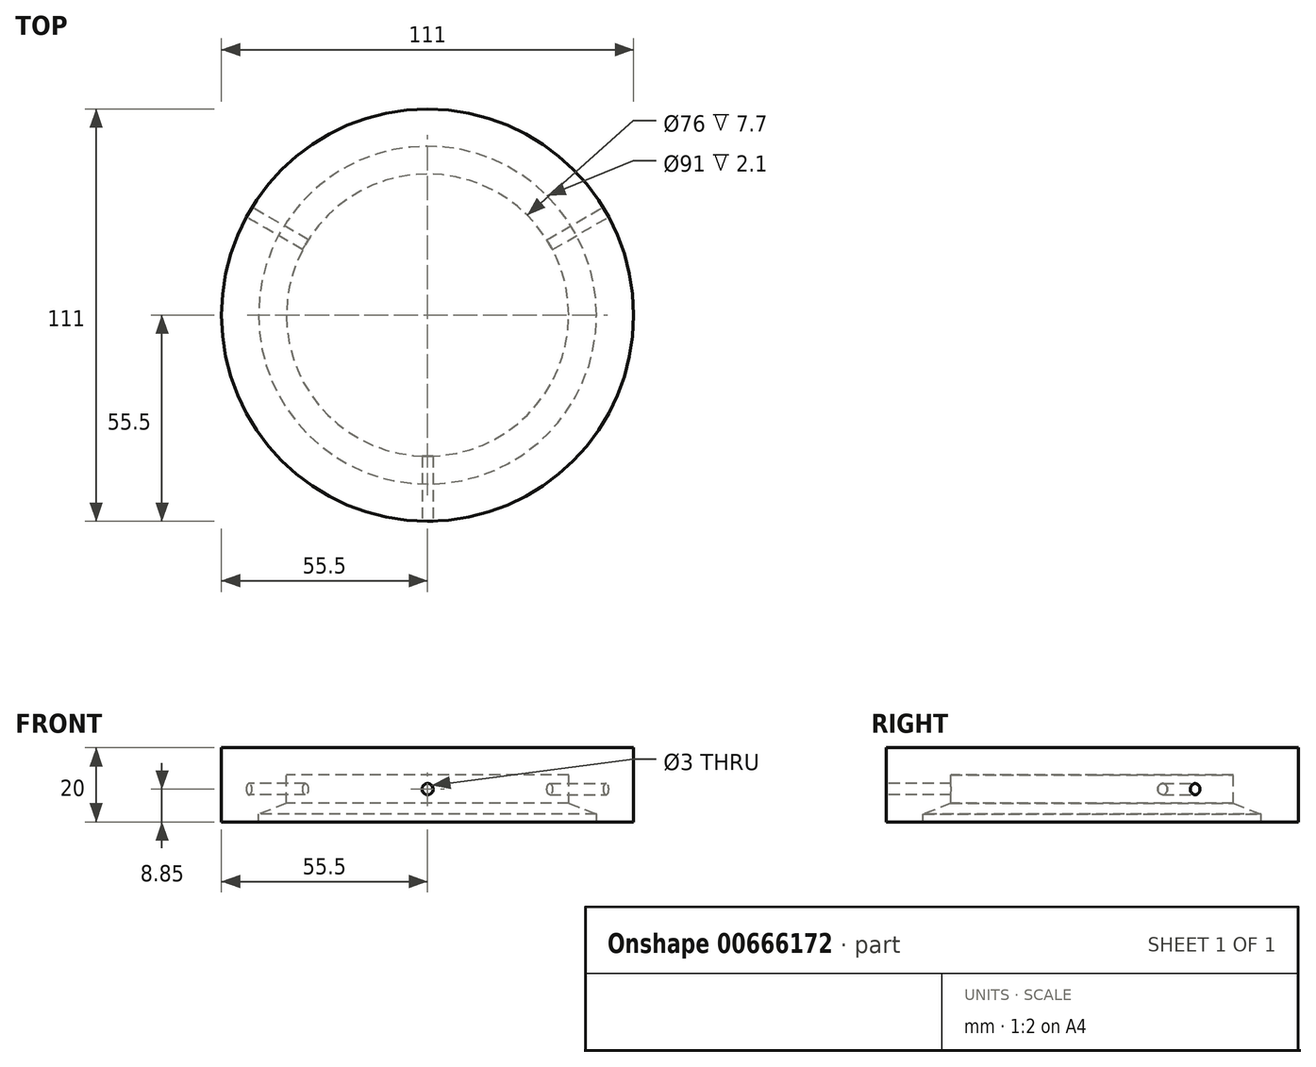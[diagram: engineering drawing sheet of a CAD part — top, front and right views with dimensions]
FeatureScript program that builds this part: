
annotation { "Feature Type Name" : "Feature", "Feature Type Description" : "" }
export const myFeature = defineFeature(function(context is Context, id is Id, definition is map)
    precondition{}
    {
        {
            var Q0;
            Q0=qCreatedBy(makeId("Right.planeOp"),FACE);
            var sketch = newSketch(context, id + "F0", { "sketchPlane" : qUnion([Q0])});
            skLineSegment(sketch, "E0", {"start": v(-45.5, 0) * mm, "end": v(-45.5, 2.1) * mm});
            skLineSegment(sketch, "E1", {"start": v(-45.5, 2.1) * mm, "end": v(-38, 5) * mm});
            skLineSegment(sketch, "E2", {"start": v(-38, 5) * mm, "end": v(-38, 12.7) * mm});
            skLineSegment(sketch, "E3", {"start": v(0, 23.43) * mm, "end": v(0, -29.1) * mm, "construction": true});
            skLineSegment(sketch, "E4", {"start": v(-55.5, 0) * mm, "end": v(-55.5, 20) * mm});
            skLineSegment(sketch, "E5", {"start": v(-38, 12.7) * mm, "end": v(0, 12.7) * mm});
            skLineSegment(sketch, "E6", {"start": v(-55.5, 20) * mm, "end": v(0, 20) * mm});
            skLineSegment(sketch, "E7", {"start": v(0, 20) * mm, "end": v(0, 12.7) * mm});
            skLineSegment(sketch, "E8", {"start": v(-45.5, 0) * mm, "end": v(-55.5, 0) * mm});
            skSolve(sketch);
        }
        {
            var Q0;
            Q0=makeQuery(id+"F0.imprint","IMPRINT",FACE,{"disambiguationData":[TD([[makeQuery(id+"F0.imprint","IMPRINT",EDGE,{"derivedFrom":sQuery(id+"F0.wireOp",EDGE,"E0")}),1.0]])]});
            var Q1;
            Q1=sQuery(id+"F0.wireOp",EDGE,"E3");
            revolve(context, id + "F1", {"entities" : qUnion([Q0]), "axis" : qUnion([Q1]), "revolveType" : RevolveType.FULL});
        }
        {
            var Q0;
            Q0=qCreatedBy(makeId("Top.planeOp"),FACE);
            cPlane(context, id + "F2", {"entities" : qUnion([Q0]), "cplaneType" : CPlaneType.OFFSET, "offset" : 8.85 * mm, "width" : 150 * mm, "height" : 150 * mm});
        }
        {
            var Q0;
            Q0=qCreatedBy(id+"F2.planeOp",FACE);
            var sketch = newSketch(context, id + "F3", { "sketchPlane" : qUnion([Q0])});
            skLineSegment(sketch, "E9", {"start": v(0, 0) * mm, "end": v(0, -55.5) * mm, "construction": true});
            skLineSegment(sketch, "E10.1.0", {"start": v(0, 0) * mm, "end": v(-48.06, 27.75) * mm, "construction": true});
            skLineSegment(sketch, "E10.2.0", {"start": v(0, 0) * mm, "end": v(48.06, 27.75) * mm, "construction": true});
            skPoint(sketch, "E10.center", {"position": v(0, 0) * mm});
            skLineSegment(sketch, "E10.anchor2", {"start": v(0, 0) * mm, "end": v(48.06, 27.75) * mm, "construction": true});
            skSolve(sketch);
        }
        {
            var Q0;
            Q0=sQuery(id+"F3.wireOp",VERTEX,"E9.end");
            var Q1;
            Q1=sQuery(id+"F3.wireOp",EDGE,"E9");
            cPlane(context, id + "F4", {"entities" : qUnion([Q0, Q1]), "cplaneType" : CPlaneType.LINE_POINT, "offset" : 25 * mm, "width" : 150 * mm, "height" : 150 * mm});
        }
        {
            var Q0;
            Q0=sQuery(id+"F3.wireOp",VERTEX,"E10.2.0.end");
            var Q1;
            Q1=sQuery(id+"F3.wireOp",EDGE,"E10.anchor2");
            cPlane(context, id + "F5", {"entities" : qUnion([Q0, Q1]), "cplaneType" : CPlaneType.LINE_POINT, "offset" : 25 * mm, "width" : 150 * mm, "height" : 150 * mm});
        }
        {
            var Q0;
            Q0=sQuery(id+"F3.wireOp",VERTEX,"E10.1.0.end");
            var Q1;
            Q1=sQuery(id+"F3.wireOp",EDGE,"E10.1.0");
            cPlane(context, id + "F6", {"entities" : qUnion([Q0, Q1]), "cplaneType" : CPlaneType.LINE_POINT, "offset" : 25 * mm, "width" : 150 * mm, "height" : 150 * mm});
        }
        {
            var Q0;
            Q0=qCreatedBy(id+"F5.planeOp",FACE);
            var sketch = newSketch(context, id + "F7", { "sketchPlane" : qUnion([Q0])});
            skCircle(sketch, "E11", {"center": v(0, 8.85) * mm, "radius": 1.5 * mm});
            skSolve(sketch);
        }
        {
            var Q0;
            Q0=qCreatedBy(id+"F6.planeOp",FACE);
            var sketch = newSketch(context, id + "F8", { "sketchPlane" : qUnion([Q0])});
            skCircle(sketch, "E12", {"center": v(0, 8.85) * mm, "radius": 1.5 * mm});
            skSolve(sketch);
        }
        {
            var Q0;
            Q0=qCreatedBy(id+"F4.planeOp",FACE);
            var sketch = newSketch(context, id + "F9", { "sketchPlane" : qUnion([Q0])});
            skCircle(sketch, "E13", {"center": v(0, 8.85) * mm, "radius": 1.5 * mm});
            skSolve(sketch);
        }
        {
            var Q0;
            Q0 = qSketchRegion(id + "F7", true);
            extrude(context, id + "F10", {"entities" : qUnion([Q0]), "operationType" : NewBodyOperationType.REMOVE, "endBound" : BoundingType.UP_TO_NEXT, "oppositeDirection" : true, "depth" : 25 * mm, "offsetDistance" : 25 * mm});
        }
        {
            var Q0;
            Q0 = qSketchRegion(id + "F8", true);
            var Q1;
            Q1=sQuery(id+"F8.wireOp",EDGE,"E12");
            extrude(context, id + "F11", {"entities" : qUnion([Q0]), "operationType" : NewBodyOperationType.REMOVE, "surfaceEntities" : qUnion([Q1]), "endBound" : BoundingType.UP_TO_NEXT, "oppositeDirection" : true, "depth" : 25 * mm, "offsetDistance" : 25 * mm});
        }
        {
            var Q0;
            Q0 = qSketchRegion(id + "F9", true);
            extrude(context, id + "F12", {"entities" : qUnion([Q0]), "operationType" : NewBodyOperationType.REMOVE, "endBound" : BoundingType.UP_TO_NEXT, "oppositeDirection" : true, "depth" : 25 * mm, "offsetDistance" : 25 * mm});
        }
    });
